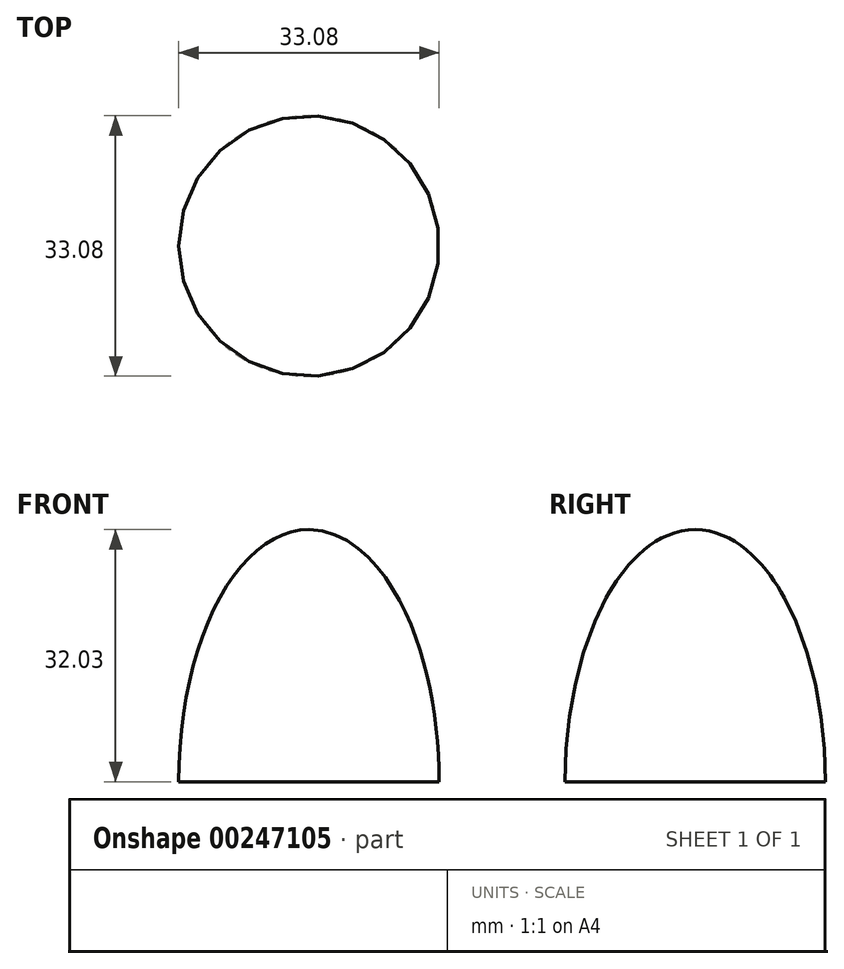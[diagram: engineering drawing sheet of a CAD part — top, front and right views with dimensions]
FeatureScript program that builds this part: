
annotation { "Feature Type Name" : "Feature", "Feature Type Description" : "" }
export const myFeature = defineFeature(function(context is Context, id is Id, definition is map)
    precondition{}
    {
        {
            var Q0;
            Q0=qCreatedBy(makeId("Front.planeOp"),FACE);
            var sketch = newSketch(context, id + "F0", { "sketchPlane" : qUnion([Q0])});
            skEllipticalArc(sketch, "E0", {});
            skLineSegment(sketch, "E1", {"start": v(0, 0) * mm, "end": v(-16.54, 0) * mm});
            skLineSegment(sketch, "E2", {"start": v(0, 32.03) * mm, "end": v(0, 0) * mm});
            const initialGuessF0  = {"E0": [0, 0, 0, 1, 0.032034363597631454, 0.01654410774037815, 0, 1.5707963267948966]};
            skSetInitialGuess(sketch, initialGuessF0);
            skSolve(sketch);
        }
        {
            var Q0;
            Q0=makeQuery(id+"F0.imprint","IMPRINT",FACE,{"disambiguationData":[TD([[makeQuery(id+"F0.imprint","IMPRINT",EDGE,{"derivedFrom":sQuery(id+"F0.wireOp",EDGE,"E0")}),1.0]])]});
            var Q1;
            Q1=sQuery(id+"F0.wireOp",EDGE,"E2");
            revolve(context, id + "F1", {"entities" : qUnion([Q0]), "axis" : qUnion([Q1]), "revolveType" : RevolveType.FULL});
        }
    });
